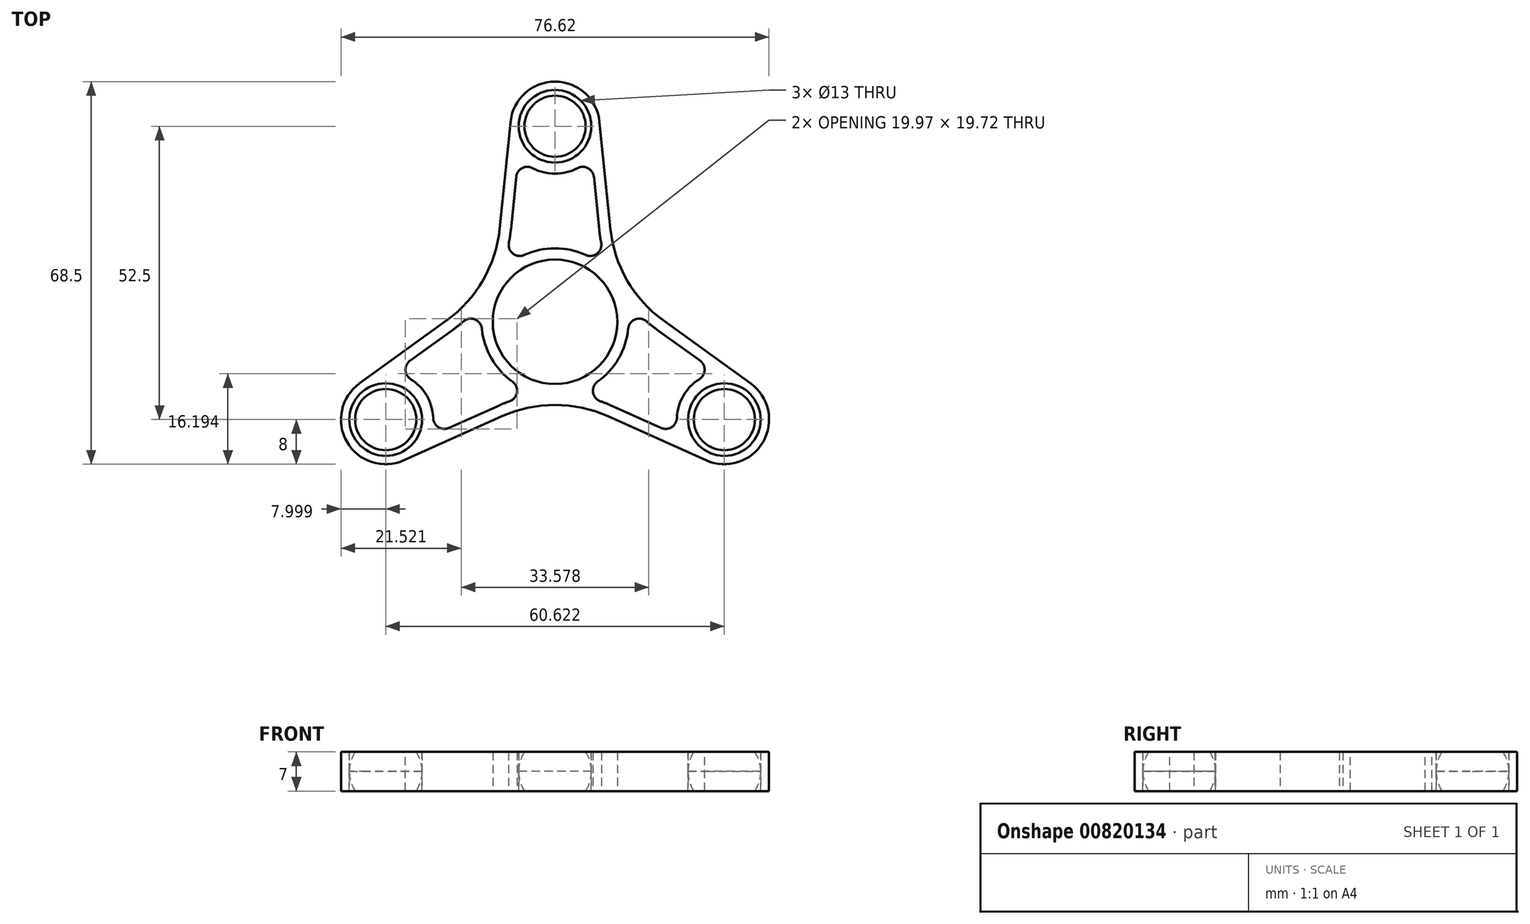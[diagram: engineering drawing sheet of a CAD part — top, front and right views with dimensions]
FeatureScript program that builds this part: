
annotation { "Feature Type Name" : "Feature", "Feature Type Description" : "" }
export const myFeature = defineFeature(function(context is Context, id is Id, definition is map)
    precondition{}
    {
        {
            var Q0;
            Q0=qCreatedBy(makeId("Top.planeOp"),FACE);
            var sketch = newSketch(context, id + "F0", { "sketchPlane" : qUnion([Q0])});
            skCircle(sketch, "E0", {"center": v(0, 0) * mm, "radius": 11.15 * mm});
            skLineSegment(sketch, "E1", {"start": v(0, 0) * mm, "end": v(0, 35) * mm});
            skCircle(sketch, "E2", {"center": v(0, 35) * mm, "radius": 6.5 * mm});
            skCircle(sketch, "E3", {"center": v(0, 35) * mm, "radius": 8 * mm});
            skCircle(sketch, "E4", {"center": v(0, 0) * mm, "radius": 12.65 * mm});
            skLineSegment(sketch, "E5", {"start": v(0, 0) * mm, "end": v(10.96, 6.33) * mm});
            skLineSegment(sketch, "E6", {"start": v(10.96, 6.33) * mm, "end": v(7.96, 35.8) * mm});
            skLineSegment(sketch, "E7.MirrorCS", {"start": v(-10.96, 6.33) * mm, "end": v(-7.96, 35.8) * mm});
            skCircle(sketch, "E8.1.0", {"center": v(-30.31, -17.5) * mm, "radius": 8 * mm});
            skLineSegment(sketch, "E8.1.1", {"start": v(-10.96, 6.33) * mm, "end": v(-35, -11.01) * mm});
            skLineSegment(sketch, "E8.1.2", {"start": v(0, -12.65) * mm, "end": v(-27.03, -24.8) * mm});
            skCircle(sketch, "E8.1.3", {"center": v(-30.31, -17.5) * mm, "radius": 6.5 * mm});
            skCircle(sketch, "E8.2.0", {"center": v(30.31, -17.5) * mm, "radius": 8 * mm});
            skLineSegment(sketch, "E8.2.1", {"start": v(0, -12.65) * mm, "end": v(27.03, -24.8) * mm});
            skLineSegment(sketch, "E8.2.2", {"start": v(10.96, 6.32) * mm, "end": v(35, -11.01) * mm});
            skCircle(sketch, "E8.2.3", {"center": v(30.31, -17.5) * mm, "radius": 6.5 * mm});
            skSolve(sketch);
        }
        {
            var Q0;
            {var subQ2=sQuery(id+"F0.wireOp",EDGE,"E8.2.1");Q0=makeQuery(id+"F0.imprint","IMPRINT",FACE,{"disambiguationData":[TD([[makeQuery(id+"F0.imprint","IMPRINT",EDGE,{"derivedFrom":subQ2}),1.0]])]});}
            var Q1;
            {var subQ2=sQuery(id+"F0.wireOp",EDGE,"E1");var subQ4=sQuery(id+"F0.wireOp",EDGE,"E0");var subQ5=makeQuery(id+"F0.imprint","INTERSECT",VERTEX,{"derivedFrom":[subQ4,subQ2]});Q1=makeQuery(id+"F0.imprint","IMPRINT",FACE,{"disambiguationData":[TD([[makeQuery(id+"F0.imprint","IMPRINT",EDGE,{"disambiguationData":[TD([[subQ5,-1.0]])],"derivedFrom":subQ4}),-1.0]])]});}
            var Q2;
            {var subQ0=sQuery(id+"F0.wireOp",EDGE,"E8.1.1");Q2=makeQuery(id+"F0.imprint","IMPRINT",FACE,{"disambiguationData":[TD([[makeQuery(id+"F0.imprint","IMPRINT",EDGE,{"derivedFrom":subQ0}),1.0]])]});}
            var Q3;
            {var subQ5=sQuery(id+"F0.wireOp",EDGE,"E6");Q3=makeQuery(id+"F0.imprint","IMPRINT",FACE,{"disambiguationData":[TD([[makeQuery(id+"F0.imprint","IMPRINT",EDGE,{"derivedFrom":subQ5}),1.0]])]});}
            var Q4;
            {var subQ0=sQuery(id+"F0.wireOp",EDGE,"E1");var subQ1=sQuery(id+"F0.wireOp",EDGE,"E0");var subQ2=makeQuery(id+"F0.imprint","INTERSECT",VERTEX,{"derivedFrom":[subQ1,subQ0]});Q4=makeQuery(id+"F0.imprint","IMPRINT",FACE,{"disambiguationData":[TD([[makeQuery(id+"F0.imprint","IMPRINT",EDGE,{"disambiguationData":[TD([[subQ2,1.0]])],"derivedFrom":subQ1}),-1.0]])]});}
            var Q5;
            {var subQ5=sQuery(id+"F0.wireOp",EDGE,"E7.MirrorCS");Q5=makeQuery(id+"F0.imprint","IMPRINT",FACE,{"disambiguationData":[TD([[makeQuery(id+"F0.imprint","IMPRINT",EDGE,{"derivedFrom":subQ5}),-1.0]])]});}
            var Q6;
            Q6=makeQuery(id+"F0.imprint","IMPRINT",FACE,{"disambiguationData":[TD([[makeQuery(id+"F0.imprint","IMPRINT",EDGE,{"derivedFrom":sQuery(id+"F0.wireOp",EDGE,"E2")}),-1.0]])]});
            var Q7;
            Q7=makeQuery(id+"F0.imprint","IMPRINT",FACE,{"disambiguationData":[TD([[makeQuery(id+"F0.imprint","IMPRINT",EDGE,{"derivedFrom":sQuery(id+"F0.wireOp",EDGE,"E8.1.3")}),-1.0]])]});
            var Q8;
            Q8=makeQuery(id+"F0.imprint","IMPRINT",FACE,{"disambiguationData":[TD([[makeQuery(id+"F0.imprint","IMPRINT",EDGE,{"derivedFrom":sQuery(id+"F0.wireOp",EDGE,"E8.2.3")}),-1.0]])]});
            extrude(context, id + "F1", {"entities" : qUnion([Q0, Q1, Q2, Q3, Q4, Q5, Q6, Q7, Q8]), "depth" : 7 * mm, "offsetDistance" : 25 * mm});
        }
        {
            var Q0;
            Q0=makeQuery(id+"F1.opExtrude","SWEPT_EDGE",EDGE,{"disambiguationData":[OSD([sQuery(id+"F0.wireOp",EDGE,"E4"),sQuery(id+"F0.wireOp",EDGE,"E8.1.2"),sQuery(id+"F0.wireOp",EDGE,"E8.2.1")])]});
            var Q1;
            Q1=makeQuery(id+"F1.opExtrude","SWEPT_EDGE",EDGE,{"disambiguationData":[OSD([sQuery(id+"F0.wireOp",EDGE,"E4"),sQuery(id+"F0.wireOp",EDGE,"E7.MirrorCS"),sQuery(id+"F0.wireOp",EDGE,"E8.1.1")])]});
            var Q2;
            Q2=makeQuery(id+"F1.opExtrude","SWEPT_EDGE",EDGE,{"disambiguationData":[OSD([sQuery(id+"F0.wireOp",EDGE,"E4"),sQuery(id+"F0.wireOp",EDGE,"E5"),sQuery(id+"F0.wireOp",EDGE,"E6"),sQuery(id+"F0.wireOp",EDGE,"E8.2.2")])]});
            fillet(context, id + "F2", {"entities" : qUnion([Q0, Q1, Q2]), "radius" : 23.2 * mm, "tangentPropagation" : true, "allowEdgeOverflow" : false});
        }
        {
            var Q0;
            Q0=makeQuery(id+"F1.opExtrude","CAP_FACE",FACE,{"disambiguationData":[OSD([sQuery(id+"F0.wireOp",EDGE,"E0"),sQuery(id+"F0.wireOp",EDGE,"E2"),sQuery(id+"F0.wireOp",EDGE,"E3"),sQuery(id+"F0.wireOp",EDGE,"E6"),sQuery(id+"F0.wireOp",EDGE,"E7.MirrorCS"),sQuery(id+"F0.wireOp",EDGE,"E8.1.0"),sQuery(id+"F0.wireOp",EDGE,"E8.1.1"),sQuery(id+"F0.wireOp",EDGE,"E8.1.2"),sQuery(id+"F0.wireOp",EDGE,"E8.1.3"),sQuery(id+"F0.wireOp",EDGE,"E8.2.0"),sQuery(id+"F0.wireOp",EDGE,"E8.2.1"),sQuery(id+"F0.wireOp",EDGE,"E8.2.2"),sQuery(id+"F0.wireOp",EDGE,"E8.2.3")])],"isStart":false});
            var sketch = newSketch(context, id + "F3", { "sketchPlane" : qUnion([Q0])});
            skCircle(sketch, "E9.0", {"center": v(0, 0) * mm, "radius": 11.15 * mm});
            skCircle(sketch, "E10.0", {"center": v(0, 35) * mm, "radius": 6.5 * mm});
            skArc(sketch, "E11.0", {"start": v(19.4, 0.23) * mm, "mid": v(12.9, 7.44) * mm, "end": v(9.9, 16.7) * mm});
            skLineSegment(sketch, "E12.0", {"start": v(9.9, 16.7) * mm, "end": v(7.96, 35.8) * mm});
            skLineSegment(sketch, "E13.0", {"start": v(-9.9, 16.7) * mm, "end": v(-7.96, 35.8) * mm});
            skArc(sketch, "E14.0", {"start": v(-9.9, 16.7) * mm, "mid": v(-12.9, 7.44) * mm, "end": v(-19.4, 0.23) * mm});
            skArc(sketch, "E15.0", {"start": v(7.96, 35.8) * mm, "mid": v(0, 43) * mm, "end": v(-7.96, 35.8) * mm});
            skLineSegment(sketch, "E16.0", {"start": v(19.4, 0.23) * mm, "end": v(35, -11.01) * mm});
            skLineSegment(sketch, "E17.0", {"start": v(9.5, -16.92) * mm, "end": v(27.03, -24.8) * mm});
            skCircle(sketch, "E18.0", {"center": v(30.31, -17.5) * mm, "radius": 6.5 * mm});
            skArc(sketch, "E19.0", {"start": v(27.03, -24.8) * mm, "mid": v(37.24, -21.5) * mm, "end": v(35, -11.01) * mm});
            skArc(sketch, "E20.0", {"start": v(-9.5, -16.92) * mm, "mid": v(0, -14.88) * mm, "end": v(9.5, -16.92) * mm});
            skLineSegment(sketch, "E21.0", {"start": v(-9.5, -16.92) * mm, "end": v(-27.03, -24.8) * mm});
            skLineSegment(sketch, "E22.0", {"start": v(-19.4, 0.23) * mm, "end": v(-35, -11.01) * mm});
            skArc(sketch, "E23.0", {"start": v(-35, -11.01) * mm, "mid": v(-37.24, -21.5) * mm, "end": v(-27.03, -24.8) * mm});
            skCircle(sketch, "E24.0", {"center": v(-30.31, -17.5) * mm, "radius": 6.5 * mm});
            skCircle(sketch, "E25", {"center": v(0, 35) * mm, "radius": 8.5 * mm});
            skCircle(sketch, "E26", {"center": v(0, 0) * mm, "radius": 13.15 * mm});
            skLineSegment(sketch, "E27.0", {"start": v(7.91, 16.5) * mm, "end": v(5.97, 35.6) * mm});
            skArc(sketch, "E27.1", {"start": v(18.24, -1.4) * mm, "mid": v(11.16, 6.44) * mm, "end": v(7.91, 16.5) * mm});
            skLineSegment(sketch, "E27.2", {"start": v(18.24, -1.4) * mm, "end": v(33.82, -12.63) * mm});
            skLineSegment(sketch, "E28.0", {"start": v(-7.91, 16.5) * mm, "end": v(-5.97, 35.6) * mm});
            skArc(sketch, "E28.1", {"start": v(-7.91, 16.5) * mm, "mid": v(-11.16, 6.44) * mm, "end": v(-18.24, -1.4) * mm});
            skLineSegment(sketch, "E28.2", {"start": v(-18.24, -1.4) * mm, "end": v(-33.82, -12.63) * mm});
            skLineSegment(sketch, "E29.0", {"start": v(-10.33, -15.1) * mm, "end": v(-27.85, -22.97) * mm});
            skArc(sketch, "E29.1", {"start": v(-10.33, -15.1) * mm, "mid": v(0, -12.88) * mm, "end": v(10.33, -15.1) * mm});
            skLineSegment(sketch, "E29.2", {"start": v(10.33, -15.1) * mm, "end": v(27.85, -22.97) * mm});
            skCircle(sketch, "E30", {"center": v(-30.31, -17.5) * mm, "radius": 8.5 * mm});
            skCircle(sketch, "E31", {"center": v(30.31, -17.5) * mm, "radius": 8.5 * mm});
            skSolve(sketch);
        }
        {
            var Q0;
            {var subQ5=sQuery(id+"F3.wireOp",EDGE,"E25");var subQ9=sQuery(id+"F3.wireOp",EDGE,"E28.0");var subQ10=makeQuery(id+"F3.imprint","INTERSECT",VERTEX,{"derivedFrom":[subQ5,subQ9]});Q0=makeQuery(id+"F3.imprint","IMPRINT",FACE,{"disambiguationData":[TD([[makeQuery(id+"F3.imprint","IMPRINT",EDGE,{"disambiguationData":[TD([[subQ10,-1.0]])],"derivedFrom":subQ5}),-1.0]])]});}
            var Q1;
            {var subQ6=sQuery(id+"F3.wireOp",EDGE,"E28.1");var subQ8=sQuery(id+"F3.wireOp",EDGE,"E26");var subQ9=makeQuery(id+"F3.imprint","INTERSECT",VERTEX,{"disambiguationData":[OD(1.0)],"derivedFrom":[subQ8,subQ6]});Q1=makeQuery(id+"F3.imprint","IMPRINT",FACE,{"disambiguationData":[TD([[makeQuery(id+"F3.imprint","IMPRINT",EDGE,{"disambiguationData":[TD([[subQ9,-1.0]])],"derivedFrom":subQ8}),-1.0]])]});}
            var Q2;
            {var subQ3=sQuery(id+"F3.wireOp",EDGE,"E26");var subQ6=sQuery(id+"F3.wireOp",EDGE,"E27.1");var subQ10=makeQuery(id+"F3.imprint","INTERSECT",VERTEX,{"disambiguationData":[OD(1.0)],"derivedFrom":[subQ3,subQ6]});Q2=makeQuery(id+"F3.imprint","IMPRINT",FACE,{"disambiguationData":[TD([[makeQuery(id+"F3.imprint","IMPRINT",EDGE,{"disambiguationData":[TD([[subQ10,1.0]])],"derivedFrom":subQ3}),-1.0]])]});}
            extrude(context, id + "F4", {"entities" : qUnion([Q0, Q1, Q2]), "operationType" : NewBodyOperationType.REMOVE, "oppositeDirection" : true, "depth" : 25 * mm, "offsetDistance" : 25 * mm});
        }
        {
            var Q0;
            {var subQ0=sQuery(id+"F3.wireOp",EDGE,"E27.1");var subQ1=sQuery(id+"F3.wireOp",EDGE,"E26");Q0=makeQuery(id+"F4.boolean.opBoolean","COPY",EDGE,{"derivedFrom":makeQuery(id+"F4.opExtrude","SWEPT_EDGE",EDGE,{"disambiguationData":[OSD([subQ1,subQ0]),TDD([makeQuery(id+"F3.imprint","INTERSECT",VERTEX,{"disambiguationData":[OD(0.0)],"derivedFrom":[subQ1,subQ0]})])]})});}
            var Q1;
            {var subQ0=sQuery(id+"F3.wireOp",EDGE,"E28.1");var subQ1=sQuery(id+"F3.wireOp",EDGE,"E26");Q1=makeQuery(id+"F4.boolean.opBoolean","COPY",EDGE,{"derivedFrom":makeQuery(id+"F4.opExtrude","SWEPT_EDGE",EDGE,{"disambiguationData":[OSD([subQ1,subQ0]),TDD([makeQuery(id+"F3.imprint","INTERSECT",VERTEX,{"disambiguationData":[OD(0.0)],"derivedFrom":[subQ1,subQ0]})])]})});}
            var Q2;
            {var subQ0=sQuery(id+"F3.wireOp",EDGE,"E28.1");var subQ1=sQuery(id+"F3.wireOp",EDGE,"E26");Q2=makeQuery(id+"F4.boolean.opBoolean","COPY",EDGE,{"derivedFrom":makeQuery(id+"F4.opExtrude","SWEPT_EDGE",EDGE,{"disambiguationData":[OSD([subQ1,subQ0]),TDD([makeQuery(id+"F3.imprint","INTERSECT",VERTEX,{"disambiguationData":[OD(1.0)],"derivedFrom":[subQ1,subQ0]})])]})});}
            var Q3;
            {var subQ0=sQuery(id+"F3.wireOp",EDGE,"E29.1");var subQ1=sQuery(id+"F3.wireOp",EDGE,"E26");Q3=makeQuery(id+"F4.boolean.opBoolean","COPY",EDGE,{"derivedFrom":makeQuery(id+"F4.opExtrude","SWEPT_EDGE",EDGE,{"disambiguationData":[OSD([subQ1,subQ0]),TDD([makeQuery(id+"F3.imprint","INTERSECT",VERTEX,{"disambiguationData":[OD(0.0)],"derivedFrom":[subQ1,subQ0]})])]})});}
            var Q4;
            {var subQ0=sQuery(id+"F3.wireOp",EDGE,"E27.1");var subQ1=sQuery(id+"F3.wireOp",EDGE,"E26");Q4=makeQuery(id+"F4.boolean.opBoolean","COPY",EDGE,{"derivedFrom":makeQuery(id+"F4.opExtrude","SWEPT_EDGE",EDGE,{"disambiguationData":[OSD([subQ1,subQ0]),TDD([makeQuery(id+"F3.imprint","INTERSECT",VERTEX,{"disambiguationData":[OD(1.0)],"derivedFrom":[subQ1,subQ0]})])]})});}
            var Q5;
            {var subQ0=sQuery(id+"F3.wireOp",EDGE,"E29.1");var subQ1=sQuery(id+"F3.wireOp",EDGE,"E26");Q5=makeQuery(id+"F4.boolean.opBoolean","COPY",EDGE,{"derivedFrom":makeQuery(id+"F4.opExtrude","SWEPT_EDGE",EDGE,{"disambiguationData":[OSD([subQ1,subQ0]),TDD([makeQuery(id+"F3.imprint","INTERSECT",VERTEX,{"disambiguationData":[OD(1.0)],"derivedFrom":[subQ1,subQ0]})])]})});}
            var Q6;
            Q6=makeQuery(id+"F4.boolean.opBoolean","COPY",EDGE,{"derivedFrom":makeQuery(id+"F4.opExtrude","SWEPT_EDGE",EDGE,{"disambiguationData":[OSD([sQuery(id+"F3.wireOp",EDGE,"E28.2"),sQuery(id+"F3.wireOp",EDGE,"E30")])]})});
            var Q7;
            Q7=makeQuery(id+"F4.boolean.opBoolean","COPY",EDGE,{"derivedFrom":makeQuery(id+"F4.opExtrude","SWEPT_EDGE",EDGE,{"disambiguationData":[OSD([sQuery(id+"F3.wireOp",EDGE,"E29.0"),sQuery(id+"F3.wireOp",EDGE,"E30")])]})});
            var Q8;
            Q8=makeQuery(id+"F4.boolean.opBoolean","COPY",EDGE,{"derivedFrom":makeQuery(id+"F4.opExtrude","SWEPT_EDGE",EDGE,{"disambiguationData":[OSD([sQuery(id+"F3.wireOp",EDGE,"E25"),sQuery(id+"F3.wireOp",EDGE,"E27.0")])]})});
            var Q9;
            Q9=makeQuery(id+"F4.boolean.opBoolean","COPY",EDGE,{"derivedFrom":makeQuery(id+"F4.opExtrude","SWEPT_EDGE",EDGE,{"disambiguationData":[OSD([sQuery(id+"F3.wireOp",EDGE,"E25"),sQuery(id+"F3.wireOp",EDGE,"E28.0")])]})});
            var Q10;
            Q10=makeQuery(id+"F4.boolean.opBoolean","COPY",EDGE,{"derivedFrom":makeQuery(id+"F4.opExtrude","SWEPT_EDGE",EDGE,{"disambiguationData":[OSD([sQuery(id+"F3.wireOp",EDGE,"E27.2"),sQuery(id+"F3.wireOp",EDGE,"E31")])]})});
            var Q11;
            Q11=makeQuery(id+"F4.boolean.opBoolean","COPY",EDGE,{"derivedFrom":makeQuery(id+"F4.opExtrude","SWEPT_EDGE",EDGE,{"disambiguationData":[OSD([sQuery(id+"F3.wireOp",EDGE,"E29.2"),sQuery(id+"F3.wireOp",EDGE,"E31")])]})});
            fillet(context, id + "F5", {"entities" : qUnion([Q0, Q1, Q2, Q3, Q4, Q5, Q6, Q7, Q8, Q9, Q10, Q11]), "radius" : 2 * mm, "tangentPropagation" : true, "allowEdgeOverflow" : false});
        }
        {
            var Q0;
            Q0=qCreatedBy(makeId("Right.planeOp"),FACE);
            var sketch = newSketch(context, id + "F6", { "sketchPlane" : qUnion([Q0])});
            skLineSegment(sketch, "E32", {"start": v(28.5, 0) * mm, "end": v(28.5, 7) * mm});
            skLineSegment(sketch, "E33", {"start": v(41.5, 7) * mm, "end": v(41.5, 0) * mm});
            skLineSegment(sketch, "E34.0", {"start": v(28.5, 7) * mm, "end": v(41.5, 7) * mm});
            skLineSegment(sketch, "E35.0", {"start": v(28.5, 0) * mm, "end": v(41.5, 0) * mm});
            skLineSegment(sketch, "E36", {"start": v(35, 7) * mm, "end": v(35, 0) * mm});
            skCircle(sketch, "E37", {"center": v(35, 3.5) * mm, "radius": 6.5 * mm});
            skLineSegment(sketch, "E38", {"start": v(0, 0) * mm, "end": v(0, 28.45) * mm});
            skSolve(sketch);
        }
        {
            var Q0;
            {var subQ0=sQuery(id+"F6.wireOp",EDGE,"E34.0");var subQ1=sQuery(id+"F6.wireOp",EDGE,"E32");var subQ2=makeQuery(id+"F6.imprint","INTERSECT",VERTEX,{"derivedFrom":[subQ1,subQ0]});Q0=makeQuery(id+"F6.imprint","IMPRINT",FACE,{"disambiguationData":[TD([[makeQuery(id+"F6.imprint","IMPRINT",EDGE,{"disambiguationData":[TD([[subQ2,1.0]])],"derivedFrom":subQ1}),-1.0]])]});}
            var Q1;
            {var subQ0=sQuery(id+"F6.wireOp",EDGE,"E35.0");var subQ1=sQuery(id+"F6.wireOp",EDGE,"E32");var subQ2=makeQuery(id+"F6.imprint","INTERSECT",VERTEX,{"derivedFrom":[subQ1,subQ0]});Q1=makeQuery(id+"F6.imprint","IMPRINT",FACE,{"disambiguationData":[TD([[makeQuery(id+"F6.imprint","IMPRINT",EDGE,{"disambiguationData":[TD([[subQ2,-1.0]])],"derivedFrom":subQ1}),-1.0]])]});}
            var Q2;
            Q2=sQuery(id+"F6.wireOp",EDGE,"E36");
            revolve(context, id + "F7", {"surfaceOperationType" : NewSurfaceOperationType.NEW, "entities" : qUnion([Q0, Q1]), "axis" : qUnion([Q2]), "revolveType" : RevolveType.FULL});
        }
        {
            var Q0;
            Q0=makeQuery(id+"F7.opRevolve","SWEPT_BODY",BODY,{"disambiguationData":[OSD([sQuery(id+"F6.wireOp",EDGE,"E32"),sQuery(id+"F6.wireOp",EDGE,"E35.0"),sQuery(id+"F6.wireOp",EDGE,"E37")])]});
            var Q1;
            Q1=makeQuery(id+"F7.opRevolve","SWEPT_BODY",BODY,{"disambiguationData":[OSD([sQuery(id+"F6.wireOp",EDGE,"E32"),sQuery(id+"F6.wireOp",EDGE,"E34.0"),sQuery(id+"F6.wireOp",EDGE,"E37")])]});
            var Q2;
            Q2=sQuery(id+"F6.wireOp",EDGE,"E38");
            circularPattern(context, id + "F8", {"entities" : qUnion([Q0, Q1]), "axis" : qUnion([Q2]), "angle" : 360 * degree, "instanceCount" : 3, "equalSpace" : true});
        }
    });
